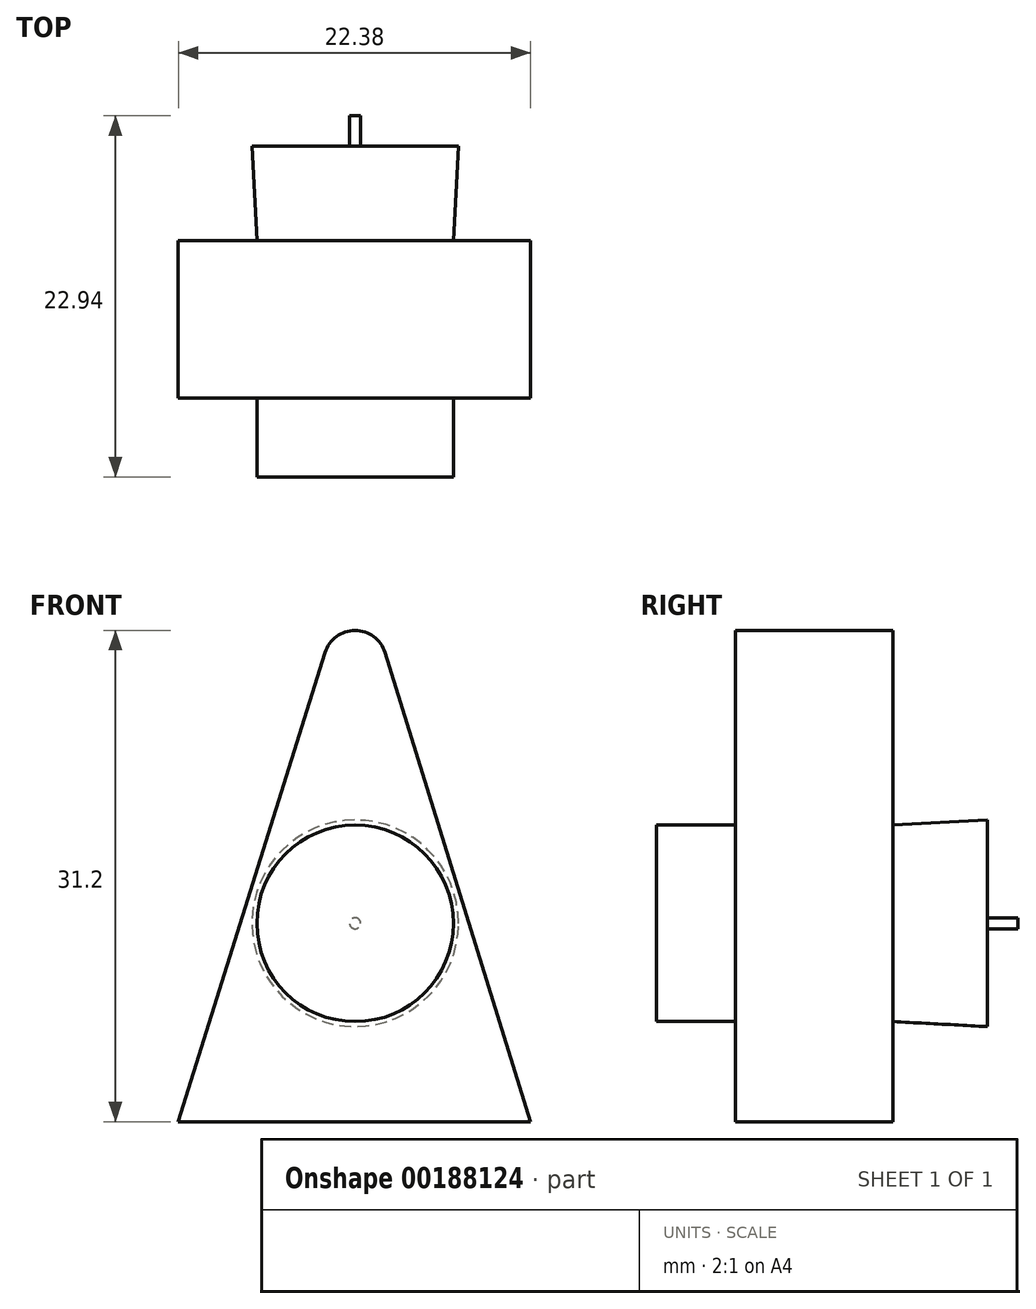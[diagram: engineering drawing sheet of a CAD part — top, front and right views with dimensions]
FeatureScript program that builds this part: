
annotation { "Feature Type Name" : "Feature", "Feature Type Description" : "" }
export const myFeature = defineFeature(function(context is Context, id is Id, definition is map)
    precondition{}
    {
        {
            var Q0;
            Q0=qCreatedBy(makeId("Front.planeOp"),FACE);
            var sketch = newSketch(context, id + "F0", { "sketchPlane" : qUnion([Q0])});
            skLineSegment(sketch, "E0", {"start": v(1.9, 17.2) * mm, "end": v(11.15, -12.6) * mm});
            skLineSegment(sketch, "E1", {"start": v(11.15, -12.6) * mm, "end": v(-11.23, -12.6) * mm});
            skLineSegment(sketch, "E2", {"start": v(-11.23, -12.6) * mm, "end": v(-1.92, 17.2) * mm});
            skPoint(sketch, "E3.visualSharp", {"position": v(0, 23.33) * mm});
            skArc(sketch, "E3.filletArc", {"start": v(1.9, 17.2) * mm, "mid": v(0, 18.6) * mm, "end": v(-1.92, 17.2) * mm});
            skCircle(sketch, "E4", {"center": v(0, 0) * mm, "radius": 6.25 * mm});
            skSolve(sketch);
        }
        {
            var Q0;
            Q0=makeQuery(id+"F0.imprint","IMPRINT",FACE,{"disambiguationData":[TD([[makeQuery(id+"F0.imprint","IMPRINT",EDGE,{"derivedFrom":sQuery(id+"F0.wireOp",EDGE,"E4")}),1.0]])]});
            var Q1;
            Q1=makeQuery(id+"F0.imprint","IMPRINT",FACE,{"disambiguationData":[TD([[makeQuery(id+"F0.imprint","IMPRINT",EDGE,{"derivedFrom":sQuery(id+"F0.wireOp",EDGE,"E0")}),-1.0]])]});
            extrude(context, id + "F3", {"entities" : qUnion([Q0, Q1]), "depth" : 10 * mm});
        }
        {
            var Q0;
            Q0=makeQuery(id+"F0.imprint","IMPRINT",FACE,{"disambiguationData":[TD([[makeQuery(id+"F0.imprint","IMPRINT",EDGE,{"derivedFrom":sQuery(id+"F0.wireOp",EDGE,"E4")}),1.0]])]});
            extrude(context, id + "F1", {"entities" : qUnion([Q0]), "operationType" : NewBodyOperationType.ADD, "depth" : 15 * mm});
        }
        {
            var Q0;
            Q0=makeQuery(id+"F0.imprint","IMPRINT",FACE,{"disambiguationData":[TD([[makeQuery(id+"F0.imprint","IMPRINT",EDGE,{"derivedFrom":sQuery(id+"F0.wireOp",EDGE,"E4")}),1.0]])]});
            extrude(context, id + "F2", {"entities" : qUnion([Q0]), "operationType" : NewBodyOperationType.ADD, "oppositeDirection" : true, "depth" : 6 * mm, "hasDraft" : true, "draftAngle" : 3 * degree});
        }
        {
            var Q0;
            Q0=makeQuery(id+"F0.imprint","IMPRINT",FACE,{"disambiguationData":[TD([[makeQuery(id+"F0.imprint","IMPRINT",EDGE,{"derivedFrom":sQuery(id+"F0.wireOp",EDGE,"E0")}),-1.0]])]});
            var sketch = newSketch(context, id + "F4", { "sketchPlane" : qUnion([Q0])});
            skCircle(sketch, "E5", {"center": v(0, 0) * mm, "radius": 0.35 * mm});
            skSolve(sketch);
        }
        {
            var Q0;
            Q0 = qSketchRegion(id + "F4", true);
            extrude(context, id + "F5", {"entities" : qUnion([Q0]), "operationType" : NewBodyOperationType.ADD, "oppositeDirection" : true, "depth" : 7.94 * mm});
        }
    });
